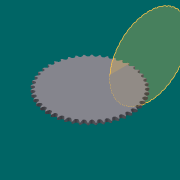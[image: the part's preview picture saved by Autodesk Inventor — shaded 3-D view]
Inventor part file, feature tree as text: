
AUTODESK INVENTOR PART (.ipt)
format: ipt  version: 2016 (Build 200138000, 138)  size: 910,336 bytes
history: native  units: mm
features: other x6, extrude x2, pattern_linear x1, pattern_circular x1
ambient origin geometry x8: Origin, YZ Plane, XZ Plane, XY Plane, X Axis, Y Axis, Z Axis, Center Point
bodies: Solid1 (feature_tree)
feature tree (10):
  other  "Theoretical Tooth Profile"
  other  "Tooth Profile"
  other  "Section Profile"
  other  "Shroud"
  other  "Strand"
  pattern_linear  "Strand Pattern"  Spacing1=186.101273mm  [1 undecoded]
  extrude  "Theoretical Tooth"  Depth=1.36591mm
  extrude  "Tooth"  Depth=3.91375mm
  pattern_circular  "Tooth Pattern"  [2 undecoded]
  other  "Timing Plane"
note: 3 required parameter values undecoded (feature->parameter linkage not recoverable at this tier; creation-order binding heuristic only, values carry confidence <= 0.55)
